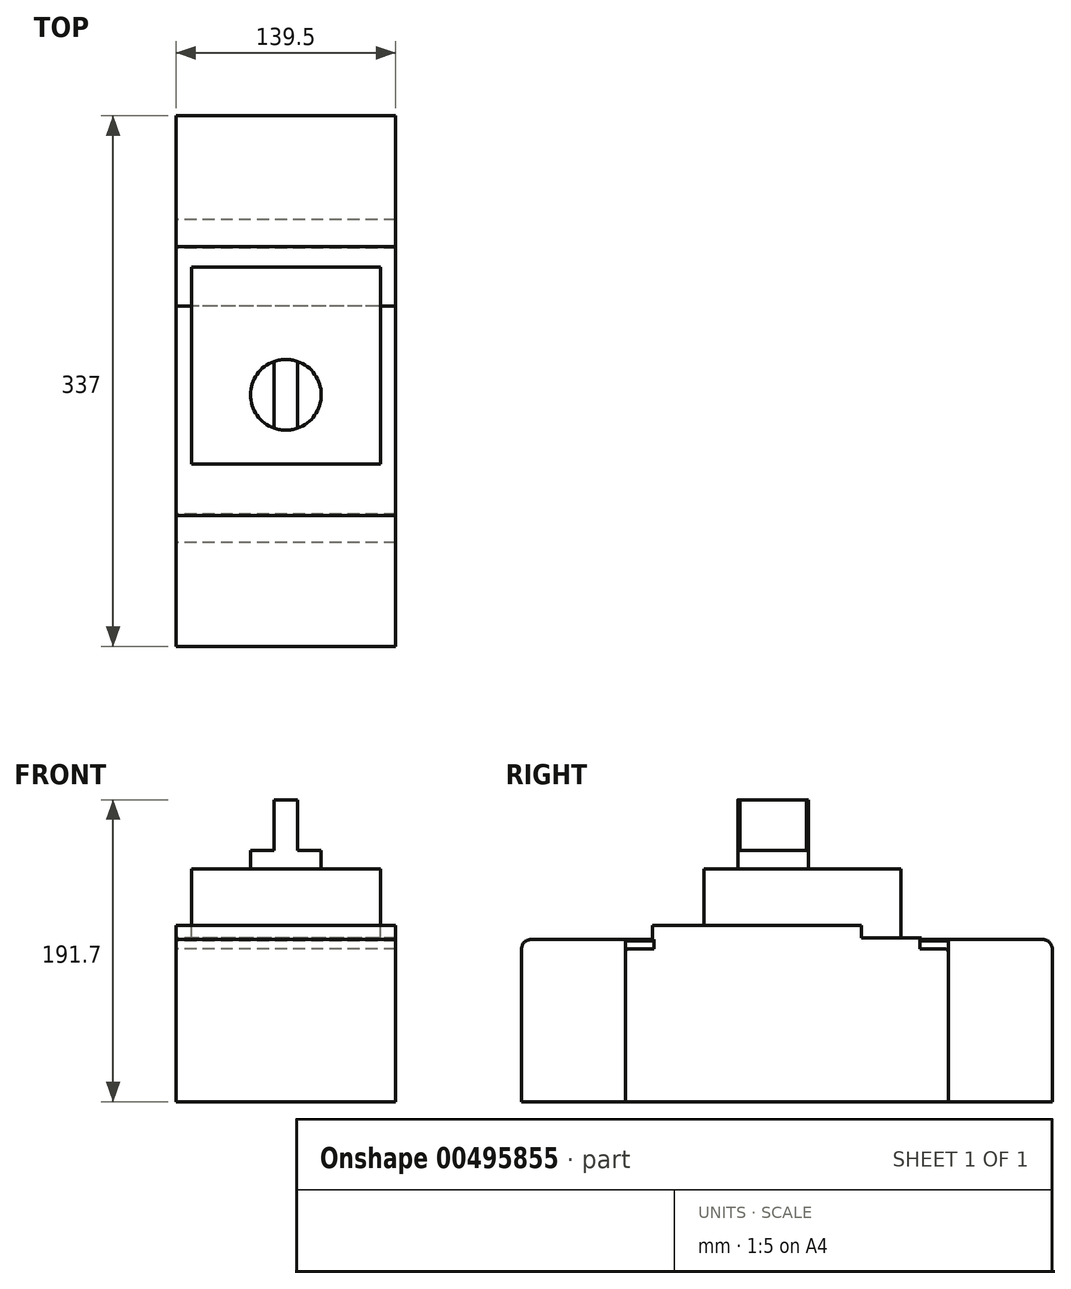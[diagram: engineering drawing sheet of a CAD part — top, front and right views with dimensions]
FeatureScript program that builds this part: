
annotation { "Feature Type Name" : "Feature", "Feature Type Description" : "" }
export const myFeature = defineFeature(function(context is Context, id is Id, definition is map)
    precondition{}
    {
        {
            var Q0;
            Q0=qCreatedBy(makeId("Right.planeOp"),FACE);
            var sketch = newSketch(context, id + "F0", { "sketchPlane" : qUnion([Q0])});
            skLineSegment(sketch, "E0", {"start": v(-102.5, 0) * mm, "end": v(102.5, 0) * mm});
            skLineSegment(sketch, "E1", {"start": v(102.5, 0) * mm, "end": v(102.5, 102) * mm});
            skLineSegment(sketch, "E2", {"start": v(102.5, 102) * mm, "end": v(85.5, 102) * mm});
            skLineSegment(sketch, "E3", {"start": v(85.5, 102) * mm, "end": v(85.5, 104) * mm});
            skLineSegment(sketch, "E4", {"start": v(85.5, 104) * mm, "end": v(47.5, 104) * mm});
            skLineSegment(sketch, "E5", {"start": v(47.5, 104) * mm, "end": v(47.5, 112) * mm});
            skLineSegment(sketch, "E6", {"start": v(47.5, 112) * mm, "end": v(-85.5, 112) * mm});
            skLineSegment(sketch, "E7", {"start": v(-85.5, 102) * mm, "end": v(-102.5, 102) * mm});
            skLineSegment(sketch, "E8", {"start": v(-102.5, 102) * mm, "end": v(-102.5, 0) * mm});
            skLineSegment(sketch, "E9", {"start": v(-85.5, 112) * mm, "end": v(-85.5, 102) * mm});
            skSolve(sketch);
        }
        {
            var Q0;
            Q0=qSketchRegion(id+"F0",true);
            extrude(context, id + "F1", {"entities" : qUnion([Q0]), "endBound" : BoundingType.SYMMETRIC, "depth" : 139.5 * mm});
        }
        {
            var Q0;
            Q0=qCreatedBy(makeId("Right.planeOp"),FACE);
            var sketch = newSketch(context, id + "F2", { "sketchPlane" : qUnion([Q0])});
            skLineSegment(sketch, "E10.0", {"start": v(85.5, 104) * mm, "end": v(47.5, 104) * mm});
            skLineSegment(sketch, "E11.0", {"start": v(47.5, 104) * mm, "end": v(47.5, 112) * mm});
            skLineSegment(sketch, "E12.0", {"start": v(47.5, 112) * mm, "end": v(-85.5, 112) * mm});
            skLineSegment(sketch, "E13", {"start": v(72.3, 104) * mm, "end": v(72.3, 147.7) * mm});
            skLineSegment(sketch, "E14", {"start": v(72.3, 147.7) * mm, "end": v(-52.7, 147.7) * mm});
            skLineSegment(sketch, "E15", {"start": v(-52.7, 147.7) * mm, "end": v(-52.7, 112) * mm});
            skSolve(sketch);
        }
        {
            var Q0;
            Q0=qSketchRegion(id+"F2",true);
            extrude(context, id + "F3", {"entities" : qUnion([Q0]), "endBound" : BoundingType.SYMMETRIC, "depth" : 120 * mm});
        }
        {
            var Q0;
            Q0=makeQuery(id+"F3.opExtrude","SWEPT_FACE",FACE,{"disambiguationData":[OSD([sQuery(id+"F2.wireOp",EDGE,"E14")])]});
            var sketch = newSketch(context, id + "F4", { "sketchPlane" : qUnion([Q0])});
            skCircle(sketch, "E16", {"center": v(0, -8.7) * mm, "radius": 22.5 * mm});
            skSolve(sketch);
        }
        {
            var Q0;
            Q0=qSketchRegion(id+"F4",true);
            extrude(context, id + "F5", {"entities" : qUnion([Q0]), "depth" : 12 * mm});
        }
        {
            var Q0;
            Q0=makeQuery(id+"F5.opExtrude","CAP_FACE",FACE,{"disambiguationData":[OSD([sQuery(id+"F4.wireOp",EDGE,"E16")])],"isStart":false});
            var sketch = newSketch(context, id + "F6", { "sketchPlane" : qUnion([Q0])});
            skCircle(sketch, "E17.0", {"center": v(0, -8.7) * mm, "radius": 22.5 * mm});
            skLineSegment(sketch, "E18", {"start": v(-7.5, 12.51) * mm, "end": v(-7.5, -29.91) * mm});
            skLineSegment(sketch, "E19", {"start": v(7.5, 12.51) * mm, "end": v(7.5, -29.91) * mm});
            skLineSegment(sketch, "E20", {"start": v(7.5, 12.51) * mm, "end": v(-7.5, -29.91) * mm, "construction": true});
            skLineSegment(sketch, "E21", {"start": v(-7.5, 12.51) * mm, "end": v(7.5, -29.91) * mm, "construction": true});
            skSolve(sketch);
        }
        {
            var Q0;
            {var subQ0=sQuery(id+"F6.wireOp",EDGE,"E18");Q0=makeQuery(id+"F6.imprint","IMPRINT",FACE,{"disambiguationData":[TD([[makeQuery(id+"F6.imprint","IMPRINT",EDGE,{"derivedFrom":subQ0}),1.0]])]});}
            extrude(context, id + "F7", {"entities" : qUnion([Q0]), "operationType" : NewBodyOperationType.ADD, "depth" : 32 * mm});
        }
        {
            var Q0;
            Q0=qCreatedBy(makeId("Right.planeOp"),FACE);
            var sketch = newSketch(context, id + "F8", { "sketchPlane" : qUnion([Q0])});
            skLineSegment(sketch, "E22", {"start": v(-46.02, 100.34) * mm, "end": v(-51.82, 112) * mm});
            skArc(sketch, "E23", {"start": v(-37.69, 105.09) * mm, "mid": v(-44.1, 106.66) * mm, "end": v(-46.02, 100.34) * mm});
            skLineSegment(sketch, "E24", {"start": v(-37.69, 105.09) * mm, "end": v(-23.07, 112) * mm});
            skLineSegment(sketch, "E25", {"start": v(-23.07, 112) * mm, "end": v(-51.82, 112) * mm});
            skLineSegment(sketch, "E26", {"start": v(-44.28, 81.88) * mm, "end": v(-44.28, 112) * mm});
            skArc(sketch, "E27", {"start": v(-2.53, 81.88) * mm, "mid": v(-23.4, 85.64) * mm, "end": v(-44.28, 81.88) * mm});
            skLineSegment(sketch, "E28", {"start": v(-2.53, 112) * mm, "end": v(-2.53, 81.88) * mm});
            skLineSegment(sketch, "E29", {"start": v(-2.53, 112) * mm, "end": v(-44.28, 112) * mm});
            skSolve(sketch);
        }
        {
            var Q0;
            Q0=qCreatedBy(makeId("Right.planeOp"),FACE);
            var sketch = newSketch(context, id + "F9", { "sketchPlane" : qUnion([Q0])});
            skLineSegment(sketch, "E30.0", {"start": v(-102.5, 102) * mm, "end": v(-102.5, 0) * mm, "construction": true});
            skLineSegment(sketch, "E31", {"start": v(-102.5, 0) * mm, "end": v(-168.5, 0) * mm});
            skLineSegment(sketch, "E32", {"start": v(-168.5, 0) * mm, "end": v(-168.5, 97) * mm});
            skLineSegment(sketch, "E33", {"start": v(-162.5, 103) * mm, "end": v(-84.5, 103) * mm});
            skLineSegment(sketch, "E34", {"start": v(-84.5, 97) * mm, "end": v(-100.5, 97) * mm});
            skLineSegment(sketch, "E35", {"start": v(-102.5, 95) * mm, "end": v(-102.5, 0) * mm});
            skPoint(sketch, "E36.visualSharp", {"position": v(-168.5, 103) * mm});
            skArc(sketch, "E36.filletArc", {"start": v(-162.5, 103) * mm, "mid": v(-166.74, 101.24) * mm, "end": v(-168.5, 97) * mm});
            skPoint(sketch, "E37.visualSharp", {"position": v(-102.5, 97) * mm});
            skArc(sketch, "E37.filletArc", {"start": v(-100.5, 97) * mm, "mid": v(-101.91, 96.41) * mm, "end": v(-102.5, 95) * mm});
            skLineSegment(sketch, "E38", {"start": v(0, 0) * mm, "end": v(0, 121.54) * mm, "construction": true});
            skLineSegment(sketch, "E39.MirrorCS", {"start": v(162.5, 103) * mm, "end": v(84.5, 103) * mm});
            skArc(sketch, "E40.MirrorCS", {"start": v(162.5, 103) * mm, "mid": v(166.74, 101.24) * mm, "end": v(168.5, 97) * mm});
            skLineSegment(sketch, "E41.MirrorCS", {"start": v(168.5, 0) * mm, "end": v(168.5, 97) * mm});
            skLineSegment(sketch, "E42.MirrorCS", {"start": v(102.5, 0) * mm, "end": v(168.5, 0) * mm});
            skLineSegment(sketch, "E43.MirrorCS", {"start": v(84.5, 97) * mm, "end": v(100.5, 97) * mm});
            skLineSegment(sketch, "E44.MirrorCS", {"start": v(84.5, 103) * mm, "end": v(84.5, 97) * mm});
            skArc(sketch, "E45.MirrorCS", {"start": v(100.5, 97) * mm, "mid": v(101.91, 96.41) * mm, "end": v(102.5, 95) * mm});
            skLineSegment(sketch, "E46.MirrorCS", {"start": v(-65, 69.3) * mm, "end": v(-65, 0) * mm, "construction": true});
            skLineSegment(sketch, "E47", {"start": v(-84.5, 103) * mm, "end": v(-84.5, 97) * mm});
            skLineSegment(sketch, "E48", {"start": v(102.5, 95) * mm, "end": v(102.5, 0) * mm});
            skSolve(sketch);
        }
        {
            var Q0;
            Q0=makeQuery(id+"F9.imprint","IMPRINT",FACE,{"disambiguationData":[TD([[makeQuery(id+"F9.imprint","IMPRINT",EDGE,{"derivedFrom":sQuery(id+"F9.wireOp",EDGE,"E31")}),-1.0]])]});
            var Q1;
            Q1=makeQuery(id+"F9.imprint","IMPRINT",FACE,{"disambiguationData":[TD([[makeQuery(id+"F9.imprint","IMPRINT",EDGE,{"derivedFrom":sQuery(id+"F9.wireOp",EDGE,"E39.MirrorCS")}),1.0]])]});
            extrude(context, id + "F10", {"entities" : qUnion([Q0, Q1]), "endBound" : BoundingType.SYMMETRIC, "depth" : 139.5 * mm});
        }
    });
